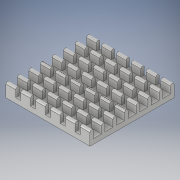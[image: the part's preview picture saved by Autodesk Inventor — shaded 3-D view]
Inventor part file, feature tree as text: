
AUTODESK INVENTOR PART (.ipt)
format: ipt  version: 2019.2 (Build 232265000, 265)  size: 323,072 bytes
history: native  units: mm
features: extrude x3, sketch x3, fillet x1
ambient origin geometry x8: Origin, YZ Plane, XZ Plane, XY Plane, X Axis, Y Axis, Z Axis, Center Point
bodies: Solid1 (feature_tree)
feature tree (7):
  extrude  "Extrusion1"  Depth=25.0mm
  extrude  "Extrusion4"  Depth=1.0mm
  fillet  "Fillet1"  Radius=2.42mm
  extrude  "Extrusion5"  Depth=1.0mm
  sketch  "Sketch1"  dims[d0=25.0mm d1=25.0mm]
  sketch  "Sketch2"  dims[d2=4.0mm d3=0.0mm d5=1.0mm d6=2.42mm]
  sketch  "Sketch3"  dims[d7=2.42mm d8=1.0mm d9=2.42mm d10=1.0mm d12=1.5mm d13=2.42mm d14=1.0mm d22=10.0mm d23=0.0mm d24=0.5mm d25=2.9167mm d26=1.5mm d27=1.5mm d28=50.0mm d30=4.4167mm d31=10.0mm d33=10.0mm d35=2.9165mm d36=10.0mm d37=0.0mm]
